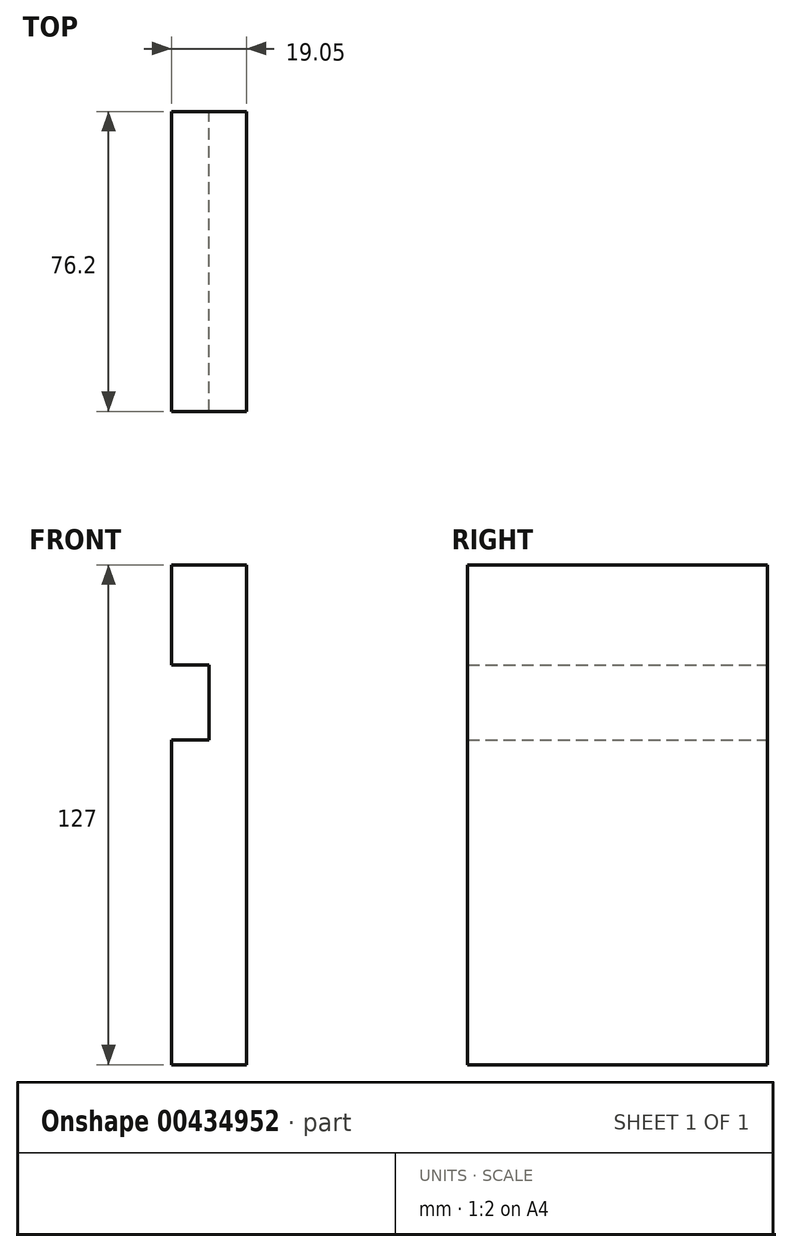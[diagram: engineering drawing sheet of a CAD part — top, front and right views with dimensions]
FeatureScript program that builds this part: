
annotation { "Feature Type Name" : "Feature", "Feature Type Description" : "" }
export const myFeature = defineFeature(function(context is Context, id is Id, definition is map)
    precondition{}
    {
        {
            var Q0;
            Q0=qCreatedBy(makeId("Front.planeOp"),FACE);
            var sketch = newSketch(context, id + "F0", { "sketchPlane" : qUnion([Q0])});
            skLineSegment(sketch, "E0", {"start": v(0, -127) * mm, "end": v(19.05, -127) * mm});
            skLineSegment(sketch, "E1", {"start": v(19.05, -127) * mm, "end": v(19.05, 0) * mm});
            skLineSegment(sketch, "E2", {"start": v(19.05, 0) * mm, "end": v(0, 0) * mm});
            skLineSegment(sketch, "E3", {"start": v(0, 0) * mm, "end": v(0, -25.4) * mm});
            skLineSegment(sketch, "E4", {"start": v(0, -25.4) * mm, "end": v(9.53, -25.4) * mm});
            skLineSegment(sketch, "E5", {"start": v(9.53, -25.4) * mm, "end": v(9.53, -44.45) * mm});
            skLineSegment(sketch, "E6", {"start": v(9.53, -44.45) * mm, "end": v(0, -44.45) * mm});
            skLineSegment(sketch, "E7", {"start": v(0, -44.45) * mm, "end": v(0, -127) * mm});
            skSolve(sketch);
        }
        {
            var Q0;
            Q0=makeQuery(id+"F0.imprint","IMPRINT",FACE,{"disambiguationData":[TD([[makeQuery(id+"F0.imprint","IMPRINT",EDGE,{"derivedFrom":sQuery(id+"F0.wireOp",EDGE,"E0")}),1.0]])]});
            extrude(context, id + "F1", {"entities" : qUnion([Q0]), "depth" : 76.2 * mm});
        }
    });
